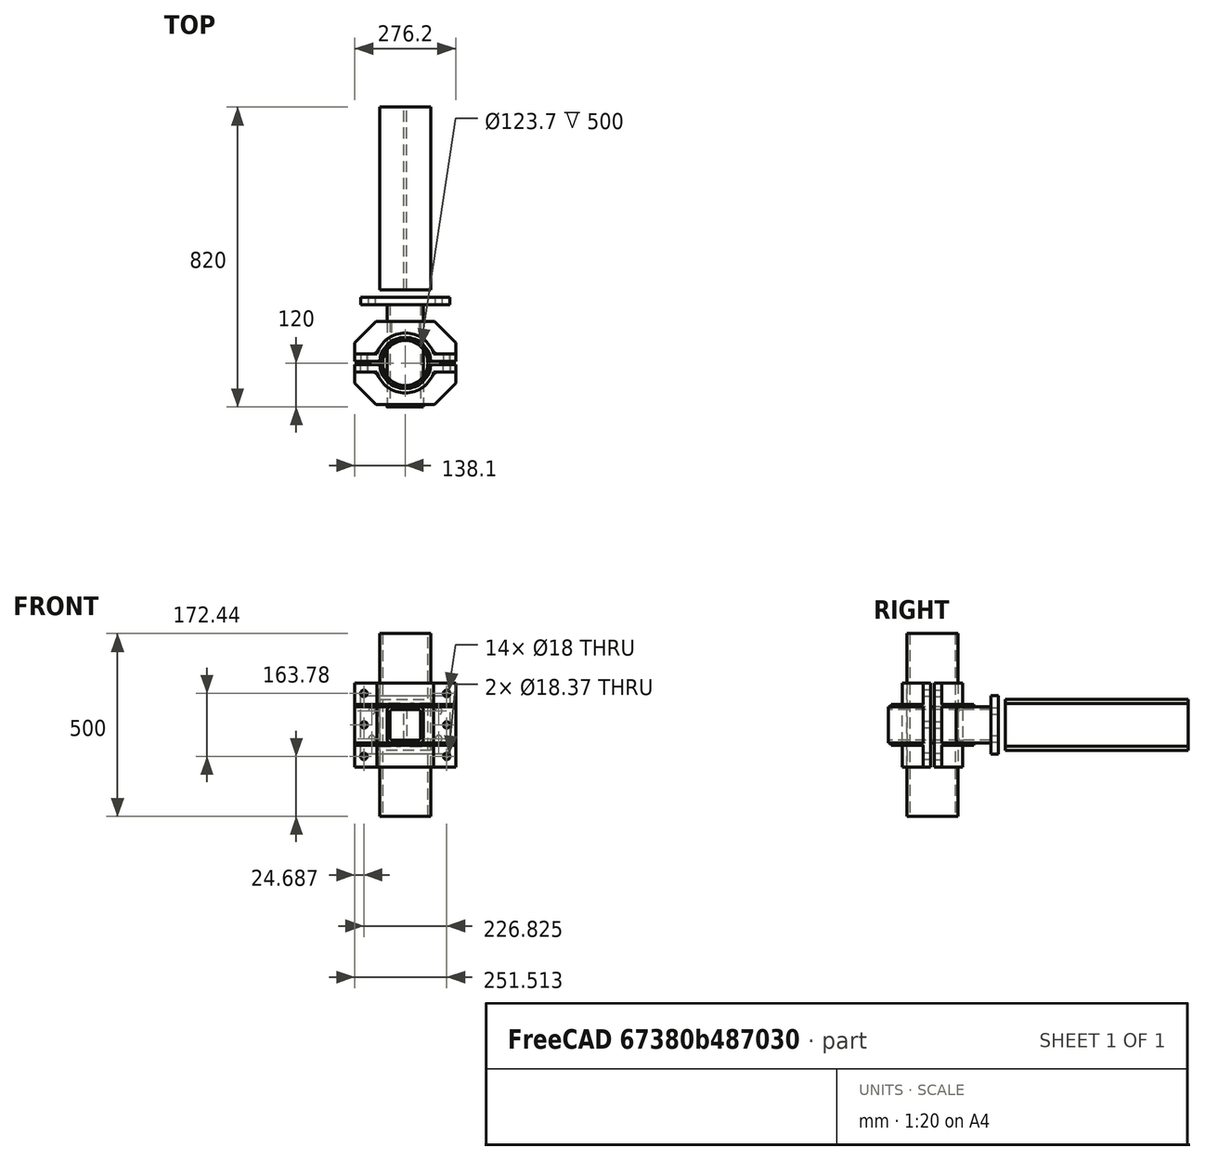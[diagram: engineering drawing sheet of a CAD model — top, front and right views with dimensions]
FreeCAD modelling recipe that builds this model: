
FCSTD DOCUMENT  (FreeCAD 0.21R33771 (Git))
Label: Schelle_fem
License: All rights reserved
LicenseURL: http://en.wikipedia.org/wiki/All_rights_reserved
objects: Part::FeaturePython×7, Sketcher::SketchObject×5, Part::Extrusion×4, Part::Feature×3, Part::MultiFuse×2, Fem::ConstraintForce×2, App::DocumentObjectGroup×1, Part::Cut×1, Fem::FemSolverObjectPython×1, App::MaterialObjectPython×1, Fem::ConstraintFixed×1, Fem::FeaturePython×1, Fem::FemMeshObjectPython×1, Fem::FemAnalysis×1
note: 22 computed .brp shape members not serialized (recipe doc carries the construction recipe); baked Part::Feature solids carry a one-line shape summary decoded from their .brp

FEATURE [Part::Feature] BOLTS_part  label="HEB140, l=500.0"
  Placement = pos=(0,0,0) rot=(-1,0,0;1.5708rad)
  shape: bbox 140 x 500 x 140 mm, 18 faces (baked)
FEATURE [Part::Feature] BOLTS_part001  label="Circular hollow profile 139.7/8.0 l=500.0"
  Placement = pos=(0,-200,-250) rot=(0,0,1;0rad)
  shape: bbox 139.7 x 139.7 x 500 mm, 4 faces (baked)
FEATURE [Part::Feature] BOLTS_part002  label="Square hollow profile 100.0/8.0 l=300.0"
  Placement = pos=(0,-20,0) rot=(1,0,0;1.5708rad)
  shape: bbox 100 x 300 x 100 mm, 18 faces (baked)
FEATURE [Sketcher::SketchObject] Sketch
  FullyConstrained = false
  Placement = pos=(0,0,0) rot=(1,0,0;1.5708rad)
  sketch-geometry (12):
    g0: LineSegment StartX=-121.553 StartY=80 StartZ=0 EndX=121.553 EndY=80 EndZ=0
    g1: LineSegment StartX=121.553 StartY=80 StartZ=0 EndX=121.553 EndY=-80 EndZ=0
    g2: LineSegment StartX=121.553 StartY=-80 StartZ=0 EndX=-121.553 EndY=-80 EndZ=0
    g3: LineSegment StartX=-121.553 StartY=-80 StartZ=0 EndX=-121.553 EndY=80 EndZ=0
    g4: LineSegment StartX=-91.5043 StartY=38.0478 StartZ=0 EndX=91.5043 EndY=38.0478 EndZ=0
    g5: LineSegment StartX=91.5043 StartY=38.0478 StartZ=0 EndX=91.5043 EndY=-38.0478 EndZ=0
    g6: LineSegment StartX=91.5043 StartY=-38.0478 StartZ=0 EndX=-91.5043 EndY=-38.0478 EndZ=0
    g7: LineSegment StartX=-91.5043 StartY=-38.0478 StartZ=0 EndX=-91.5043 EndY=38.0478 EndZ=0
    g8: Circle CenterX=91.5043 CenterY=38.0478 CenterZ=0 NormalX=0 NormalY=0 NormalZ=1 AngleXU=0 Radius=9
    g9: Circle CenterX=91.5043 CenterY=-38.0478 CenterZ=0 NormalX=0 NormalY=0 NormalZ=1 AngleXU=0 Radius=9
    g10: Circle CenterX=-91.5043 CenterY=38.0478 CenterZ=0 NormalX=0 NormalY=0 NormalZ=1 AngleXU=0 Radius=9
    g11: Circle CenterX=-91.5043 CenterY=-38.0478 CenterZ=0 NormalX=0 NormalY=0 NormalZ=1 AngleXU=0 Radius=9
  constraints (25):
    c: Coincident(g0,g1)
    c: Coincident(g1,g2)
    c: Coincident(g2,g3)
    c: Coincident(g3,g0)
    c: Horizontal(g0)
    c: Vertical(g3)
    c: Symmetric(g1,g0,g-1)
    c: Symmetric(g2,g1,g-2)
    c: DistanceY(g1,g1) = 160
    c: Coincident(g4,g5)
    c: Coincident(g5,g6)
    c: Coincident(g6,g7)
    c: Coincident(g7,g4)
    c: Horizontal(g4)
    c: Vertical(g7)
    c: Symmetric(g5,g4,g-1)
    c: Symmetric(g6,g5,g-2)
    c: Coincident(g8,g4)
    c: Coincident(g9,g5)
    c: Coincident(g10,g4)
    c: Coincident(g11,g6)
    c: Equal(g9,g8)
    c: Equal(g9,g10)
    c: Equal(g9,g11)
    c: Diameter(g9) = 18
FEATURE [Part::Extrusion] Extrude  label="flansch"
  Base = -> Sketch
  Dir = (0,-1,0)
  DirMode = 0
  FaceMakerClass = Part::FaceMakerBullseye
  LengthFwd = 20
  LengthRev = 0
  Solid = true
  Symmetric = false
FEATURE [Sketcher::SketchObject] Sketch001
  ExternalGeometry = -> [BOLTS_part001]
  FullyConstrained = true
  sketch-geometry (10):
    g0: ArcOfCircle CenterX=0 CenterY=-200 CenterZ=0 NormalX=0 NormalY=0 NormalZ=1 AngleXU=0 Radius=82 StartAngle=0.30981 EndAngle=2.83178
    g1: ArcOfCircle CenterX=0 CenterY=-200 CenterZ=0 NormalX=0 NormalY=0 NormalZ=1 AngleXU=0 Radius=70 StartAngle=0.0714894 EndAngle=3.0701
    g2: LineSegment StartX=-78.0961 StartY=-175 StartZ=0 EndX=-138.096 EndY=-175 EndZ=0
    g3: LineSegment StartX=-138.096 StartY=-175 StartZ=0 EndX=-138.096 EndY=-195 EndZ=0
    g4: LineSegment StartX=-138.096 StartY=-195 StartZ=0 EndX=-69.8212 EndY=-195 EndZ=0
    g5: LineSegment StartX=-78.0961 StartY=-175 StartZ=0 EndX=-66.6674 EndY=-178.659 EndZ=0
    g6: LineSegment StartX=0 StartY=-200 StartZ=0 EndX=-138.096 EndY=-200 EndZ=0
    g7: LineSegment StartX=69.8212 StartY=-195 StartZ=0 EndX=138.096 EndY=-195 EndZ=0
    g8: LineSegment StartX=138.096 StartY=-195 StartZ=0 EndX=138.096 EndY=-175 EndZ=0
    g9: LineSegment StartX=138.096 StartY=-175 StartZ=0 EndX=78.0961 EndY=-175 EndZ=0
  constraints (30):
    c: Coincident(g0,g-3)
    c: Coincident(g1,g0)
    c: Diameter(g1) = 140
    c: Coincident(g0,g2)
    c: Horizontal(g2)
    c: Coincident(g2,g3)
    c: Coincident(g3,g4)
    c: Horizontal(g4)
    c: Vertical(g3)
    c: Coincident(g4,g1)
    c: DistanceY(g3,g3) = 20
    c: Coincident(g5,g0)
    c: PointOnObject(g5,g1)
    c: Perpendicular(g1,g5)
    c: Distance(g5) = 12
    c: Coincident(g6,g0)
    c: Horizontal(g6)
    c: Vertical(g6,g3)
    c: DistanceY(g6,g3) = 5
    c: DistanceX(g2,g2) = 60
    c: Coincident(g1,g7)
    c: Horizontal(g7)
    c: Coincident(g7,g8)
    c: Vertical(g8)
    c: Coincident(g8,g9)
    c: Horizontal(g9)
    c: Horizontal(g1,g1)
    c: Equal(g2,g9)
    c: Equal(g3,g8)
    c: Coincident(g0,g9)
FEATURE [Part::Extrusion] Extrude001  label="schellenblech"
  Base = -> Sketch001
  Dir = (0,0,1)
  DirMode = 0
  FaceMakerClass = Part::FaceMakerBullseye
  LengthFwd = 230
  LengthRev = 0
  Solid = true
  Symmetric = true
FEATURE [Part::FeaturePython] Clone  label="flansch001"  # Draft clone (typed FeaturePython)
  AttacherType = Attacher::AttachEngine3D
  Fuse = false
  Objects = -> [Extrude]
  Placement = pos=(0,-20,0) rot=(0,0,1;0rad)
  Scale = (1,1,1)
FEATURE [Part::FeaturePython] Facebinder  # WARN: FeaturePython — macro-defined, semantics opaque (R4)
  Area = 47564.4
  Extrusion = 0
  Faces = -> [Extrude001]
  RemoveSplitter = false
  Sew = false
FEATURE [Part::FeaturePython] Slice  # WARN: FeaturePython — macro-defined, semantics opaque (R4)
  Base = -> BOLTS_part002
  Mode = 1
  Tolerance = 0
  Tools = -> [Facebinder]
FEATURE [Part::FeaturePython] Slice_child0  label="Slice.0"  # WARN: FeaturePython — macro-defined, semantics opaque (R4)
  Base = -> Slice
  FilterType = 1
  Invert = false
  OverrideMaxVal = 0
  WindowFrom = 80
  WindowTo = 100
  items = 0
FEATURE [Part::FeaturePython] Slice_child1  label="Slice.1"  # WARN: FeaturePython — macro-defined, semantics opaque (R4)
  Base = -> Slice
  FilterType = 1
  Invert = false
  OverrideMaxVal = 0
  WindowFrom = 80
  WindowTo = 100
  items = 1
FEATURE [App::DocumentObjectGroup] GrExplode_Slice  label="Exploded Slice"
  Group = -> [Slice_child1]
FEATURE [Sketcher::SketchObject] Sketch002
  ExternalGeometry = -> [Extrude001,BOLTS_part001]
  FullyConstrained = true
  sketch-geometry (10):
    g0: LineSegment StartX=-138.096 StartY=-175 StartZ=0 EndX=-138.096 EndY=-145 EndZ=0
    g1: LineSegment StartX=-138.096 StartY=-145 StartZ=0 EndX=-80 EndY=-86.9039 EndZ=0
    g2: LineSegment StartX=-80 StartY=-86.9039 StartZ=0 EndX=80 EndY=-86.9039 EndZ=0
    g3: LineSegment StartX=80 StartY=-86.9039 StartZ=0 EndX=138.096 EndY=-145 EndZ=0
    g4: LineSegment StartX=138.096 StartY=-145 StartZ=0 EndX=138.096 EndY=-175 EndZ=0
    g5: LineSegment StartX=138.096 StartY=-175 StartZ=0 EndX=86.0961 EndY=-175 EndZ=0
    g6: LineSegment StartX=-138.096 StartY=-175 StartZ=0 EndX=-86.0961 EndY=-175 EndZ=0
    g7: LineSegment StartX=-86.0961 StartY=-175 StartZ=0 EndX=-74.3449 EndY=-167.222 EndZ=0
    g8: LineSegment StartX=86.0961 StartY=-175 StartZ=0 EndX=74.3449 EndY=-167.222 EndZ=0
    g9: ArcOfCircle CenterX=0 CenterY=-200 CenterZ=0 NormalX=0 NormalY=0 NormalZ=1 AngleXU=0 Radius=81.25 StartAngle=0.415252 EndAngle=2.72634
  constraints (27):
    c: Coincident(g-4,g0)
    c: Vertical(g0)
    c: Coincident(g0,g1)
    c: Coincident(g1,g2)
    c: Coincident(g2,g3)
    c: Coincident(g3,g4)
    c: Coincident(g4,g-3)
    c: Vertical(g4)
    c: Coincident(g4,g5)
    c: Horizontal(g5)
    c: Coincident(g6,g0)
    c: Horizontal(g6)
    c: Equal(g0,g4)
    c: DistanceY(g4,g4) = 30
    c: Symmetric(g1,g2,g-2)
    c: Angle(g0,g1) = 2.35619
    c: DistanceX(g2,g2) = 160
    c: Coincident(g7,g6)
    c: Coincident(g8,g5)
    c: Coincident(g9,g-5)
    c: Coincident(g9,g7)
    c: Coincident(g9,g8)
    c: Diameter(g9) = 162.5
    c: Equal(g6,g5)
    c: DistanceX(g6,g6) = 52
    c: Equal(g7,g8)
    c: Angle(g5,g8) = 2.55691
FEATURE [Part::Extrusion] Extrude002
  Base = -> Sketch002
  Dir = (0,0,1)
  DirMode = 0
  FaceMakerClass = Part::FaceMakerBullseye
  LengthFwd = 6
  LengthRev = 0
  Placement = pos=(0,0,50) rot=(0,0,1;0rad)
  Solid = true
  Symmetric = false
FEATURE [Part::FeaturePython] Clone001  label="Extrude003"  # Draft clone (typed FeaturePython)
  AttacherType = Attacher::AttachEngine3D
  Fuse = false
  Objects = -> [Extrude002]
  Placement = pos=(0,0,-56) rot=(0,0,1;0rad)
  Scale = (1,1,1)
FEATURE [Sketcher::SketchObject] Sketch003
  ExternalGeometry = -> [Extrude001]
  FullyConstrained = false
  MapMode = 5
  Placement = pos=(0,-175,0) rot=(0,0.707107,0.707107;3.14159rad)
  Support = -> [Extrude001]
  sketch-geometry (17):
    g0: Circle CenterX=-113.413 CenterY=86.22 CenterZ=0 NormalX=0 NormalY=0 NormalZ=1 AngleXU=0 Radius=9
    g1: Circle CenterX=-113.413 CenterY=-86.22 CenterZ=0 NormalX=0 NormalY=0 NormalZ=1 AngleXU=0 Radius=9.18475
    g2: Circle CenterX=113.413 CenterY=-86.22 CenterZ=0 NormalX=0 NormalY=0 NormalZ=1 AngleXU=0 Radius=9
    g3: Circle CenterX=113.413 CenterY=86.22 CenterZ=0 NormalX=0 NormalY=0 NormalZ=1 AngleXU=0 Radius=9
    g4: Circle CenterX=112.569 CenterY=0 CenterZ=0 NormalX=0 NormalY=0 NormalZ=1 AngleXU=0 Radius=9
    g5: Circle CenterX=-113.413 CenterY=0 CenterZ=0 NormalX=0 NormalY=0 NormalZ=1 AngleXU=0 Radius=9
    g6: LineSegment StartX=-113.413 StartY=86.22 StartZ=0 EndX=-113.413 EndY=-86.22 EndZ=0
    g7: LineSegment StartX=113.413 StartY=86.22 StartZ=0 EndX=113.413 EndY=-86.22 EndZ=0
    g8: LineSegment StartX=-113.413 StartY=86.22 StartZ=0 EndX=113.413 EndY=86.22 EndZ=0
    g9: LineSegment StartX=-113.413 StartY=-86.22 StartZ=0 EndX=113.413 EndY=-86.22 EndZ=0
    g10: LineSegment StartX=-113.413 StartY=86.22 StartZ=0 EndX=-142.096 EndY=106.277 EndZ=0
    g11: LineSegment StartX=-113.413 StartY=-86.22 StartZ=0 EndX=-138.096 EndY=-115 EndZ=0
    g12: LineSegment StartX=113.413 StartY=-86.22 StartZ=0 EndX=138.096 EndY=-115 EndZ=0
    g13: LineSegment StartX=113.413 StartY=86.22 StartZ=0 EndX=133.33 EndY=115 EndZ=0
    g14: LineSegment StartX=-113.413 StartY=86.22 StartZ=0 EndX=-113.413 EndY=115 EndZ=0
    g15: LineSegment StartX=113.413 StartY=86.22 StartZ=0 EndX=113.413 EndY=115 EndZ=0
    g16: LineSegment StartX=113.413 StartY=-86.22 StartZ=0 EndX=113.413 EndY=-115 EndZ=0
  constraints (39):
    c: Equal(g0,g5)
    c: Equal(g0,g2)
    c: Equal(g0,g4)
    c: Equal(g0,g3)
    c: Diameter(g0) = 18
    c: Coincident(g6,g0)
    c: Coincident(g6,g1)
    c: Vertical(g6)
    c: Coincident(g7,g3)
    c: Coincident(g7,g2)
    c: Vertical(g7)
    c: Coincident(g8,g0)
    c: Coincident(g8,g3)
    c: Horizontal(g8)
    c: Coincident(g9,g1)
    c: Coincident(g9,g2)
    c: Horizontal(g9)
    c: Coincident(g10,g0)
    c: Coincident(g11,g1)
    c: Coincident(g11,g-4)
    c: Coincident(g12,g2)
    c: Coincident(g12,g-6)
    c: Coincident(g13,g3)
    c: PointOnObject(g13,g-5)
    c: Equal(g10,g13)
    c: Equal(g11,g12)
    c: Distance(g10) = 35
    c: Coincident(g14,g0)
    c: PointOnObject(g14,g-3)
    c: Vertical(g14)
    c: Coincident(g15,g3)
    c: PointOnObject(g15,g-5)
    c: Vertical(g15)
    c: Coincident(g16,g2)
    c: PointOnObject(g16,g-6)
    c: Vertical(g16)
    c: Symmetric(g6,g6,g5)
    c: Horizontal(g5,g-1)
    c: Horizontal(g-1,g4)
FEATURE [Part::Extrusion] Extrude003  label="Loch"
  Base = -> Sketch003
  Dir = (0,-1,0)
  DirMode = 0
  FaceMakerClass = Part::FaceMakerBullseye
  LengthFwd = 60
  LengthRev = 0
  Solid = true
  Symmetric = true
FEATURE [Part::Cut] Cut
  Base = -> Extrude001
  Tool = -> Extrude003
FEATURE [Part::MultiFuse] Fusion  label="Schelle"
  Shapes = -> [Clone001,Extrude002,Cut]
FEATURE [Part::FeaturePython] Clone002  label="Schelle001"  # Draft clone (typed FeaturePython)
  AttacherType = Attacher::AttachEngine3D
  Fuse = false
  Objects = -> [Fusion]
  Placement = pos=(0,-400,0) rot=(1,0,0;3.14159rad)
  Scale = (1,1,1)
FEATURE [Sketcher::SketchObject] Sketch004
  FullyConstrained = false
  MapMode = 5
  Placement = pos=(0,500,1.11e-13) rot=(-1,0,0;1.5708rad)
  Support = -> [BOLTS_part]
  sketch-geometry (14):
    g0: LineSegment StartX=0.135599 StartY=-0.0219419 StartZ=0 EndX=0.433662 EndY=0.305485 EndZ=0
    g1: LineSegment StartX=0.433662 StartY=0.305485 StartZ=0 EndX=0.299133 EndY=0.727328 EndZ=0
    g2: LineSegment StartX=0.299133 StartY=0.727328 StartZ=0 EndX=-0.133458 EndY=0.821744 EndZ=0
    g3: LineSegment StartX=-0.133458 StartY=0.821744 StartZ=0 EndX=-0.431521 EndY=0.494318 EndZ=0
    g4: LineSegment StartX=-0.431521 StartY=0.494318 StartZ=0 EndX=-0.296992 EndY=0.0724743 EndZ=0
    g5: LineSegment StartX=-0.296992 StartY=0.0724743 StartZ=0 EndX=0.135599 EndY=-0.0219419 EndZ=0
    g6: Circle CenterX=0.00107051 CenterY=0.399901 CenterZ=0 NormalX=0 NormalY=0 NormalZ=1 AngleXU=0 Radius=0.442775
    g7: LineSegment StartX=-5.50953 StartY=118.124 StartZ=0 EndX=-104.408 EndY=54.8169 EndZ=0
    g8: LineSegment StartX=-104.408 StartY=54.8169 StartZ=0 EndX=-99.0318 EndY=-62.485 EndZ=0
    g9: LineSegment StartX=-99.0318 StartY=-62.485 StartZ=0 EndX=5.24261 EndY=-116.48 EndZ=0
    g10: LineSegment StartX=5.24261 StartY=-116.48 StartZ=0 EndX=104.141 EndY=-53.1734 EndZ=0
    g11: LineSegment StartX=104.141 StartY=-53.1734 StartZ=0 EndX=98.7649 EndY=64.1285 EndZ=0
    g12: LineSegment StartX=98.7649 StartY=64.1285 StartZ=0 EndX=-5.50953 EndY=118.124 EndZ=0
    g13: Circle CenterX=-0.133458 CenterY=0.821744 CenterZ=0 NormalX=0 NormalY=0 NormalZ=1 AngleXU=0 Radius=117.425
  constraints (27):
    c: Coincident(g0,g1)
    c: Coincident(g1,g2)
    c: Coincident(g2,g3)
    c: Coincident(g3,g4)
    c: Coincident(g4,g5)
    c: Coincident(g5,g0)
    c: Equal(g0, g1-g5) x5
    c: PointOnObject(g0,g6)
    c: PointOnObject(g1,g6)
    c: PointOnObject(g2,g6)
    c: PointOnObject(g3,g6)
    c: PointOnObject(g4,g6)
    c: PointOnObject(g5,g6)
    c: Coincident(g7,g8)
    c: Coincident(g8,g9)
    c: Coincident(g9,g10)
    c: Coincident(g10,g11)
    c: Coincident(g11,g12)
    c: Coincident(g12,g7)
    c: Equal(g7, g8-g12) x5
    c: PointOnObject(g7,g13)
    c: PointOnObject(g8,g13)
    c: PointOnObject(g9,g13)
    c: PointOnObject(g10,g13)
    c: PointOnObject(g11,g13)
    c: PointOnObject(g12,g13)
    c: Coincident(g13,g2)
FEATURE [Fem::FemSolverObjectPython] SolverCcxTools  # FEM object (typed FeaturePython)
  AnalysisType = 0
  BeamShellResultOutput3D = false
  BucklingFactors = 1
  EigenmodeHighLimit = 1000000
  EigenmodeLowLimit = 0
  EigenmodesCount = 10
  GeometricalNonlinearity = 0
  IterationsControlParameterCutb = 0.25,0.5,0.75,0.85,,,1.5,
  IterationsControlParameterIter = 4,8,9,200,10,400,,200,,
  IterationsControlParameterTimeUse = false
  IterationsThermoMechMaximum = 2000
  IterationsUserDefinedIncrementations = false
  IterationsUserDefinedTimeStepLength = false
  MaterialNonlinearity = 0
  MatrixSolverType = 0
  SplitInputWriter = true
  ThermoMechSteadyState = true
  TimeEnd = 1
  TimeInitialStep = 0.01
FEATURE [App::MaterialObjectPython] MaterialSolid  label="S235"  # material (typed FeaturePython)
  Category = 0
  Material = AuthorAndLicense=(c) 2013 Juergen Riegel (CC-BY 3.0),CardName=CalculiX-Steel,Density=7900 kg/m^3,+8 more (map truncated)
FEATURE [Part::MultiFuse] Fusion001  label="KlemmeFEM"
  Refine = true
  Shapes = -> [Fusion,Slice_child0,Clone]
FEATURE [Fem::ConstraintFixed] ConstraintFixed
  NormalDirection = (-1,0,-1e-16)
  Normals = (72) [(1,0,0),(-0.5,-1.90526e-16,-0.866025),(-0.5,1.90526e-16,0.866025),(1,5.38845e-32,2.44929e-16),(1,0,0),(-0.5,-1.90526e-16,-0.866025),+66 more]
  Points = (72) [(104.413,-195,86.22),(117.913,-195,94.0142),(117.913,-195,78.4257),(104.413,-195,86.22),(104.413,-185,86.22),(117.913,-185,94.0142),+66 more]
  References = -> [Fusion001]
  Scale = 5
FEATURE [Fem::ConstraintForce] ConstraintForce001
  Direction = -> Extrude [Edge2]
  DirectionVector = (0,-1,0)
  Force = 47000
  NormalDirection = (0,0,1)
  Points = (12) [(-121.553,-40,80),(-40.5175,-40,80),(40.5175,-40,80),(121.553,-40,80),(-121.553,-30,80),(-40.5175,-30,80),(40.5175,-30,80),(121.553,-30,80),+4 more]
  References = -> [Fusion001]
  Scale = 12
FEATURE [Fem::FeaturePython] MeshRegion  # FEM object (typed FeaturePython)
  CharacteristicLength = 3
  References = -> [Fusion001]
FEATURE [Fem::FemMeshObjectPython] FEMMeshGmsh  # FEM object (typed FeaturePython)
  Algorithm2D = 0
  Algorithm3D = 0
  CharacteristicLengthMax = 10
  CharacteristicLengthMin = 0
  CoherenceMesh = true
  ElementDimension = 3
  ElementOrder = 1
  GeometryTolerance = 1e-06
  GroupsOfNodes = false
  HighOrderOptimize = 0
  MeshRegionList = -> [MeshRegion]
  MeshSizeFromCurvature = 12
  OptimizeNetgen = false
  OptimizeStd = true
  Part = -> Fusion001
  RecombinationAlgorithm = 0
  Recombine3DAll = false
  RecombineAll = false
  SecondOrderLinear = false
FEATURE [Fem::ConstraintForce] ConstraintForce
  Direction = -> Extrude [Edge5]
  DirectionVector = (0,1,0)
  Force = 47000
  NormalDirection = (0,0,-1)
  Points = (12) [(121.553,-40,-80),(40.5175,-40,-80),(-40.5175,-40,-80),(-121.553,-40,-80),(121.553,-30,-80),(40.5175,-30,-80),(-40.5175,-30,-80),(-121.553,-30,-80),+4 more]
  References = -> [Fusion001]
  Reversed = true
  Scale = 12
FEATURE [Fem::FemAnalysis] Analysis
  Group = -> [SolverCcxTools,MaterialSolid,ConstraintFixed,ConstraintForce001,FEMMeshGmsh,ConstraintForce]
